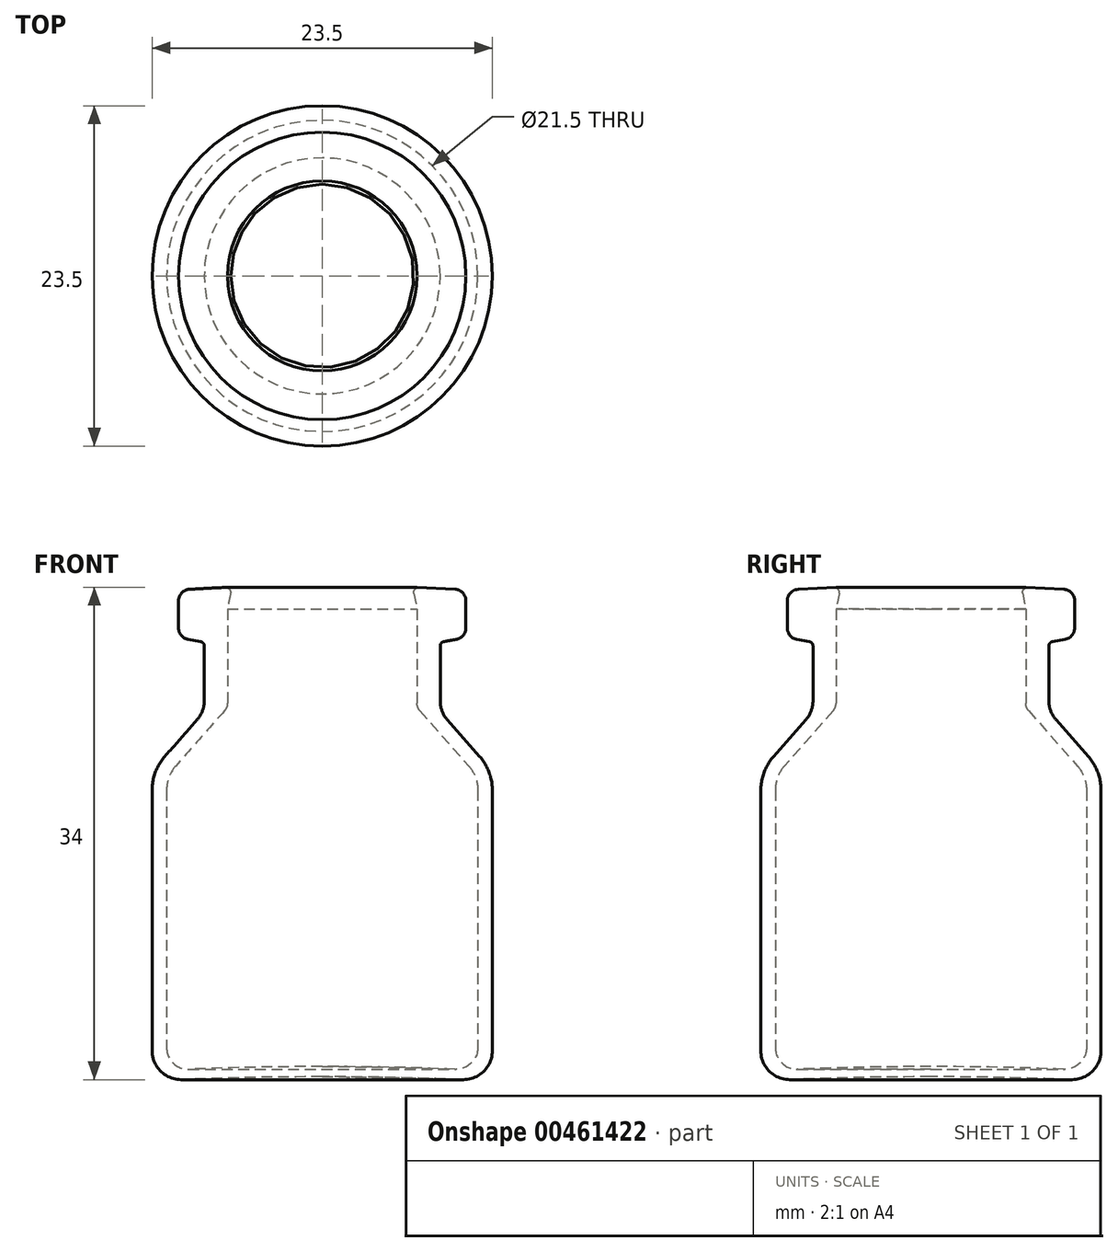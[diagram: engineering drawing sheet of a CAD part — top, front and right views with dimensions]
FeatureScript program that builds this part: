
annotation { "Feature Type Name" : "Feature", "Feature Type Description" : "" }
export const myFeature = defineFeature(function(context is Context, id is Id, definition is map)
    precondition{}
    {
        {
            var Q0;
            Q0=qCreatedBy(makeId("Front.planeOp"),FACE);
            var sketch = newSketch(context, id + "F0", { "sketchPlane" : qUnion([Q0])});
            skLineSegment(sketch, "E0", {"start": v(0, -1.48) * mm, "end": v(0, 36.05) * mm, "construction": true});
            skLineSegment(sketch, "E1", {"start": v(11.75, 2) * mm, "end": v(11.75, 20) * mm});
            skLineSegment(sketch, "E2", {"start": v(10.87, 22.32) * mm, "end": v(8.65, 24.83) * mm});
            skLineSegment(sketch, "E3", {"start": v(8.15, 26.16) * mm, "end": v(8.15, 30.2) * mm});
            skLineSegment(sketch, "E4", {"start": v(8.15, 30.2) * mm, "end": v(9.26, 30.4) * mm});
            skLineSegment(sketch, "E5", {"start": v(9.93, 31.19) * mm, "end": v(9.93, 33.82) * mm});
            skLineSegment(sketch, "E6", {"start": v(9.93, 33.82) * mm, "end": v(6.55, 34) * mm});
            skLineSegment(sketch, "E7", {"start": v(6.3, 33.75) * mm, "end": v(6.55, 32.5) * mm});
            skLineSegment(sketch, "E8", {"start": v(6.55, 32.5) * mm, "end": v(6.55, 25.7) * mm});
            skArc(sketch, "E9", {"start": v(11.75, 2) * mm, "mid": v(11.13, 0.56) * mm, "end": v(9.67, 0) * mm});
            skArc(sketch, "E10", {"start": v(9.67, 0) * mm, "mid": v(4.84, 0.15) * mm, "end": v(0, 0.2) * mm});
            skLineSegment(sketch, "E11", {"start": v(13.36, 0) * mm, "end": v(-2.46, 0) * mm, "construction": true});
            skLineSegment(sketch, "E12", {"start": v(0, 0.2) * mm, "end": v(-2.86, 0.2) * mm, "construction": true});
            skLineSegment(sketch, "E13", {"start": v(0, 0.9) * mm, "end": v(0, 0.2) * mm});
            skArc(sketch, "E14.0", {"start": v(9.2, 0.72) * mm, "mid": v(4.6, 0.86) * mm, "end": v(0, 0.9) * mm});
            skLineSegment(sketch, "E15", {"start": v(6.55, 34) * mm, "end": v(6.3, 33.75) * mm});
            skPoint(sketch, "E16.visualSharp", {"position": v(8.15, 25.4) * mm});
            skArc(sketch, "E16.filletArc", {"start": v(8.15, 26.16) * mm, "mid": v(8.28, 25.45) * mm, "end": v(8.65, 24.83) * mm});
            skLineSegment(sketch, "E17", {"start": v(8.15, 30.2) * mm, "end": v(13, 30.2) * mm, "construction": true});
            skPoint(sketch, "E18.visualSharp", {"position": v(11.75, 21.32) * mm});
            skArc(sketch, "E18.filletArc", {"start": v(11.75, 20) * mm, "mid": v(11.52, 21.24) * mm, "end": v(10.87, 22.32) * mm});
            skLineSegment(sketch, "E19", {"start": v(6.55, 34) * mm, "end": v(13.71, 34) * mm, "construction": true});
            skLineSegment(sketch, "E20", {"start": v(5.53, 38.33) * mm, "end": v(5.53, 33.7) * mm, "construction": true});
            skPoint(sketch, "E21.visualSharp", {"position": v(9.92, 30.52) * mm});
            skArc(sketch, "E21.filletArc", {"start": v(9.26, 30.4) * mm, "mid": v(9.74, 30.67) * mm, "end": v(9.92, 31.19) * mm});
            skLineSegment(sketch, "E22.0", {"start": v(10.12, 21.66) * mm, "end": v(6.55, 25.7) * mm});
            skArc(sketch, "E22.1", {"start": v(10.75, 20) * mm, "mid": v(10.59, 20.88) * mm, "end": v(10.12, 21.66) * mm});
            skLineSegment(sketch, "E22.2", {"start": v(10.75, 2.22) * mm, "end": v(10.75, 20) * mm});
            skPoint(sketch, "E23.visualSharp", {"position": v(10.75, 0.66) * mm});
            skArc(sketch, "E23.filletArc", {"start": v(9.2, 0.72) * mm, "mid": v(10.29, 1.14) * mm, "end": v(10.75, 2.22) * mm});
            skSolve(sketch);
        }
        {
            var Q0;
            Q0=makeQuery(id+"F0.imprint","IMPRINT",FACE,{"disambiguationData":[TD([[makeQuery(id+"F0.imprint","IMPRINT",EDGE,{"derivedFrom":sQuery(id+"F0.wireOp",EDGE,"E1")}),1.0]])]});
            var Q1;
            Q1=sQuery(id+"F0.wireOp",EDGE,"E0");
            revolve(context, id + "F1", {"entities" : qUnion([Q0]), "axis" : qUnion([Q1]), "revolveType" : RevolveType.FULL});
        }
        {
            var Q0;
            Q0=makeQuery(id+"F1.opRevolve","SWEPT_EDGE",EDGE,{"disambiguationData":[OSD([sQuery(id+"F0.wireOp",EDGE,"E5"),sQuery(id+"F0.wireOp",EDGE,"E6")])]});
            var Q1;
            Q1=makeQuery(id+"F1.opRevolve","SWEPT_EDGE",EDGE,{"disambiguationData":[OSD([sQuery(id+"F0.wireOp",EDGE,"E8"),sQuery(id+"F0.wireOp",EDGE,"E22.0")])]});
            fillet(context, id + "F2", {"entities" : qUnion([Q0, Q1]), "radius" : .8 * mm, "tangentPropagation" : true, "allowEdgeOverflow" : false});
        }
        {
            var Q0;
            Q0=makeQuery(id+"F1.opRevolve","SWEPT_EDGE",EDGE,{"disambiguationData":[OSD([sQuery(id+"F0.wireOp",EDGE,"E3"),sQuery(id+"F0.wireOp",EDGE,"E4")])]});
            var Q1;
            Q1=makeQuery(id+"F1.opRevolve","SWEPT_EDGE",EDGE,{"disambiguationData":[OSD([sQuery(id+"F0.wireOp",EDGE,"E7"),sQuery(id+"F0.wireOp",EDGE,"E15")])]});
            fillet(context, id + "F3", {"entities" : qUnion([Q0, Q1]), "radius" : .3 * mm, "tangentPropagation" : true, "allowEdgeOverflow" : false});
        }
    });
